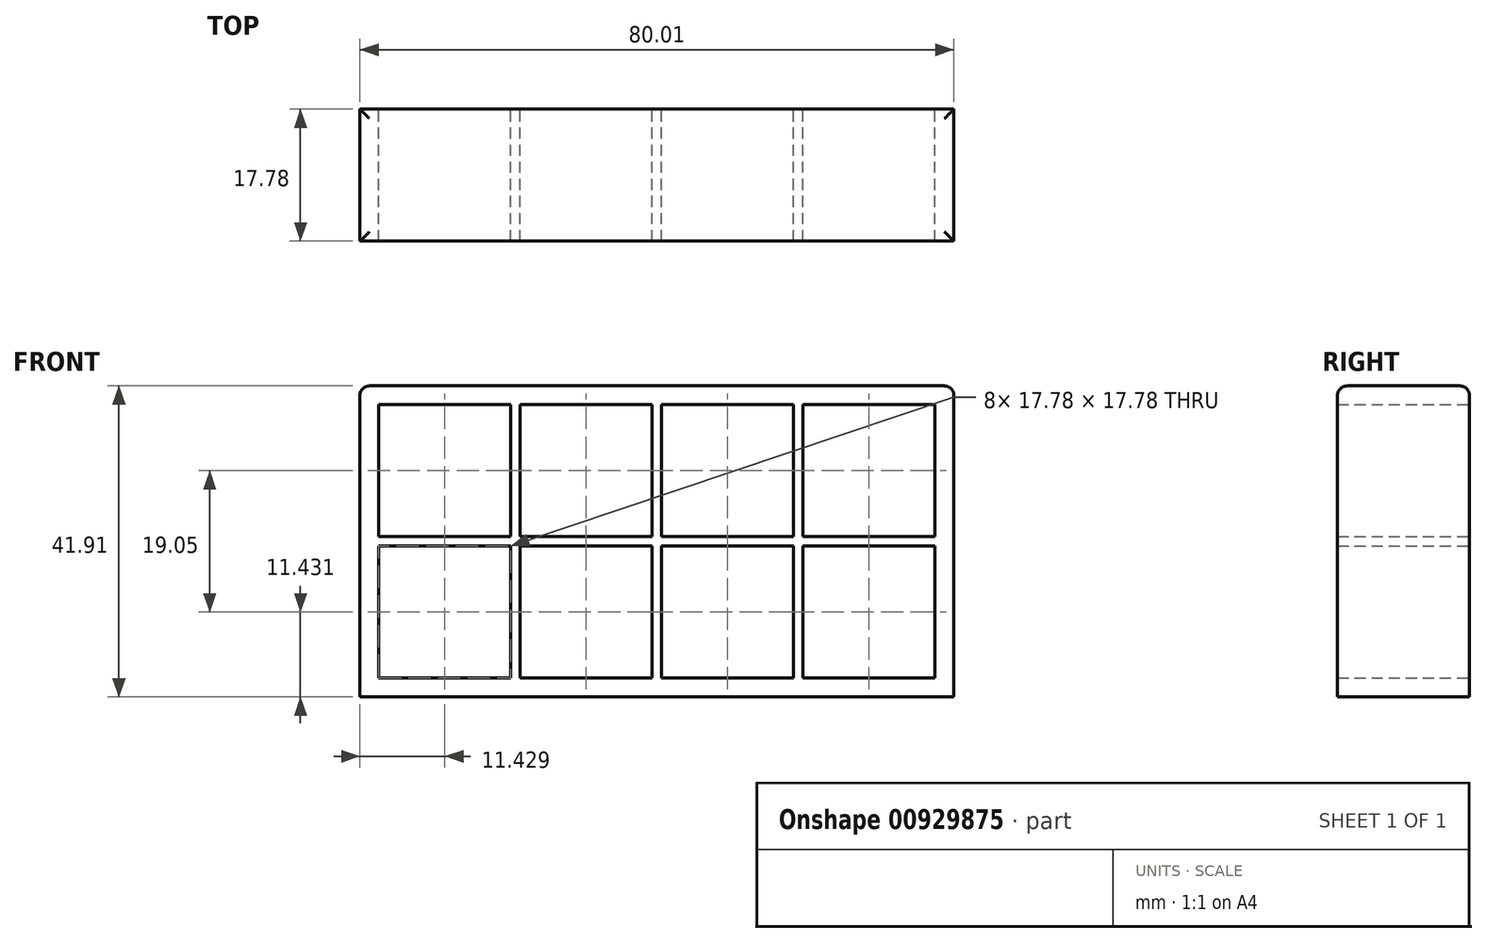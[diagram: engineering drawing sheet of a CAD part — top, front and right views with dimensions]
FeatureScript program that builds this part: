
annotation { "Feature Type Name" : "Feature", "Feature Type Description" : "" }
export const myFeature = defineFeature(function(context is Context, id is Id, definition is map)
    precondition{}
    {
        {
            var Q0;
            Q0=qCreatedBy(makeId("Front.planeOp"),FACE);
            var sketch = newSketch(context, id + "F0", { "sketchPlane" : qUnion([Q0])});
            skLineSegment(sketch, "E0.bottom", {"start": v(-38.03, 44.34) * mm, "end": v(-20.25, 44.34) * mm});
            skLineSegment(sketch, "E0.top", {"start": v(-38.03, 26.56) * mm, "end": v(-20.25, 26.56) * mm});
            skLineSegment(sketch, "E0.left", {"start": v(-38.03, 44.34) * mm, "end": v(-38.03, 26.56) * mm});
            skLineSegment(sketch, "E0.right", {"start": v(-20.25, 44.34) * mm, "end": v(-20.25, 26.56) * mm});
            skLineSegment(sketch, "E1.bottom", {"start": v(-38.03, 25.3) * mm, "end": v(-20.25, 25.3) * mm});
            skLineSegment(sketch, "E1.top", {"start": v(-38.03, 7.51) * mm, "end": v(-20.25, 7.51) * mm});
            skLineSegment(sketch, "E1.left", {"start": v(-38.03, 25.3) * mm, "end": v(-38.03, 7.51) * mm});
            skLineSegment(sketch, "E1.right", {"start": v(-20.25, 25.3) * mm, "end": v(-20.25, 7.51) * mm});
            skLineSegment(sketch, "E2.bottom", {"start": v(-18.98, 25.3) * mm, "end": v(-1.2, 25.3) * mm});
            skLineSegment(sketch, "E2.top", {"start": v(-18.98, 7.51) * mm, "end": v(-1.2, 7.51) * mm});
            skLineSegment(sketch, "E2.left", {"start": v(-18.98, 25.3) * mm, "end": v(-18.98, 7.51) * mm});
            skLineSegment(sketch, "E2.right", {"start": v(-1.2, 25.3) * mm, "end": v(-1.2, 7.51) * mm});
            skLineSegment(sketch, "E3.bottom", {"start": v(0.07, 25.3) * mm, "end": v(17.85, 25.3) * mm});
            skLineSegment(sketch, "E3.top", {"start": v(0.07, 7.51) * mm, "end": v(17.85, 7.51) * mm});
            skLineSegment(sketch, "E3.left", {"start": v(0.07, 25.3) * mm, "end": v(0.07, 7.51) * mm});
            skLineSegment(sketch, "E3.right", {"start": v(17.85, 25.3) * mm, "end": v(17.85, 7.51) * mm});
            skLineSegment(sketch, "E4.bottom", {"start": v(19.12, 25.3) * mm, "end": v(36.9, 25.3) * mm});
            skLineSegment(sketch, "E4.top", {"start": v(19.12, 7.51) * mm, "end": v(36.9, 7.51) * mm});
            skLineSegment(sketch, "E4.left", {"start": v(19.12, 25.3) * mm, "end": v(19.12, 7.51) * mm});
            skLineSegment(sketch, "E4.right", {"start": v(36.9, 25.3) * mm, "end": v(36.9, 7.51) * mm});
            skLineSegment(sketch, "E5.bottom", {"start": v(-63.43, -17.89) * mm, "end": v(-63.43, 6.8) * mm});
            skLineSegment(sketch, "E5.top", {"start": v(-39, -17.89) * mm, "end": v(60.05, -17.89) * mm});
            skLineSegment(sketch, "E5.left", {"start": v(-63.43, 6.8) * mm, "end": v(-63.43, 4.7) * mm});
            skLineSegment(sketch, "E5.right", {"start": v(-63.43, -17.89) * mm, "end": v(60.05, -17.89) * mm});
            skLineSegment(sketch, "E6.bottom", {"start": v(-18.98, 44.34) * mm, "end": v(-1.2, 44.34) * mm});
            skLineSegment(sketch, "E6.top", {"start": v(-18.98, 26.56) * mm, "end": v(-1.2, 26.56) * mm});
            skLineSegment(sketch, "E6.left", {"start": v(-18.98, 44.34) * mm, "end": v(-18.98, 26.56) * mm});
            skLineSegment(sketch, "E6.right", {"start": v(-1.2, 44.34) * mm, "end": v(-1.2, 26.56) * mm});
            skLineSegment(sketch, "E7.bottom", {"start": v(0.07, 26.56) * mm, "end": v(17.85, 26.56) * mm});
            skLineSegment(sketch, "E7.top", {"start": v(0.07, 44.34) * mm, "end": v(17.85, 44.34) * mm});
            skLineSegment(sketch, "E7.left", {"start": v(0.07, 26.56) * mm, "end": v(0.07, 44.34) * mm});
            skLineSegment(sketch, "E7.right", {"start": v(17.85, 26.56) * mm, "end": v(17.85, 44.34) * mm});
            skLineSegment(sketch, "E8.bottom", {"start": v(19.12, 26.56) * mm, "end": v(36.9, 26.56) * mm});
            skLineSegment(sketch, "E8.top", {"start": v(19.12, 44.34) * mm, "end": v(36.9, 44.34) * mm});
            skLineSegment(sketch, "E8.left", {"start": v(19.12, 26.56) * mm, "end": v(19.12, 44.34) * mm});
            skLineSegment(sketch, "E8.right", {"start": v(36.9, 26.56) * mm, "end": v(36.9, 44.34) * mm});
            skLineSegment(sketch, "E9.bottom", {"start": v(-40.57, 46.88) * mm, "end": v(39.44, 46.88) * mm});
            skLineSegment(sketch, "E9.top", {"start": v(-40.57, 4.97) * mm, "end": v(39.44, 4.97) * mm});
            skLineSegment(sketch, "E9.left", {"start": v(-40.57, 46.88) * mm, "end": v(-40.57, 4.97) * mm});
            skLineSegment(sketch, "E9.right", {"start": v(39.44, 46.88) * mm, "end": v(39.44, 4.97) * mm});
            skSolve(sketch);
        }
        {
            var Q0;
            Q0=makeQuery(id+"F0.imprint","IMPRINT",FACE,{"disambiguationData":[TD([[makeQuery(id+"F0.imprint","IMPRINT",EDGE,{"derivedFrom":sQuery(id+"F0.wireOp",EDGE,"E0.bottom")}),1.0]])]});
            extrude(context, id + "F1", {"entities" : qUnion([Q0]), "depth" : 17.78 * mm, "offsetDistance" : 25.4 * mm});
        }
        {
            var Q0;
            Q0=makeQuery(id+"F1.opExtrude","SWEPT_FACE",FACE,{"disambiguationData":[OSD([sQuery(id+"F0.wireOp",EDGE,"E9.bottom")])]});
            fillet(context, id + "F2", {"entities" : qUnion([Q0]), "radius" : 1.27 * mm, "tangentPropagation" : true, "allowEdgeOverflow" : false});
        }
    });
